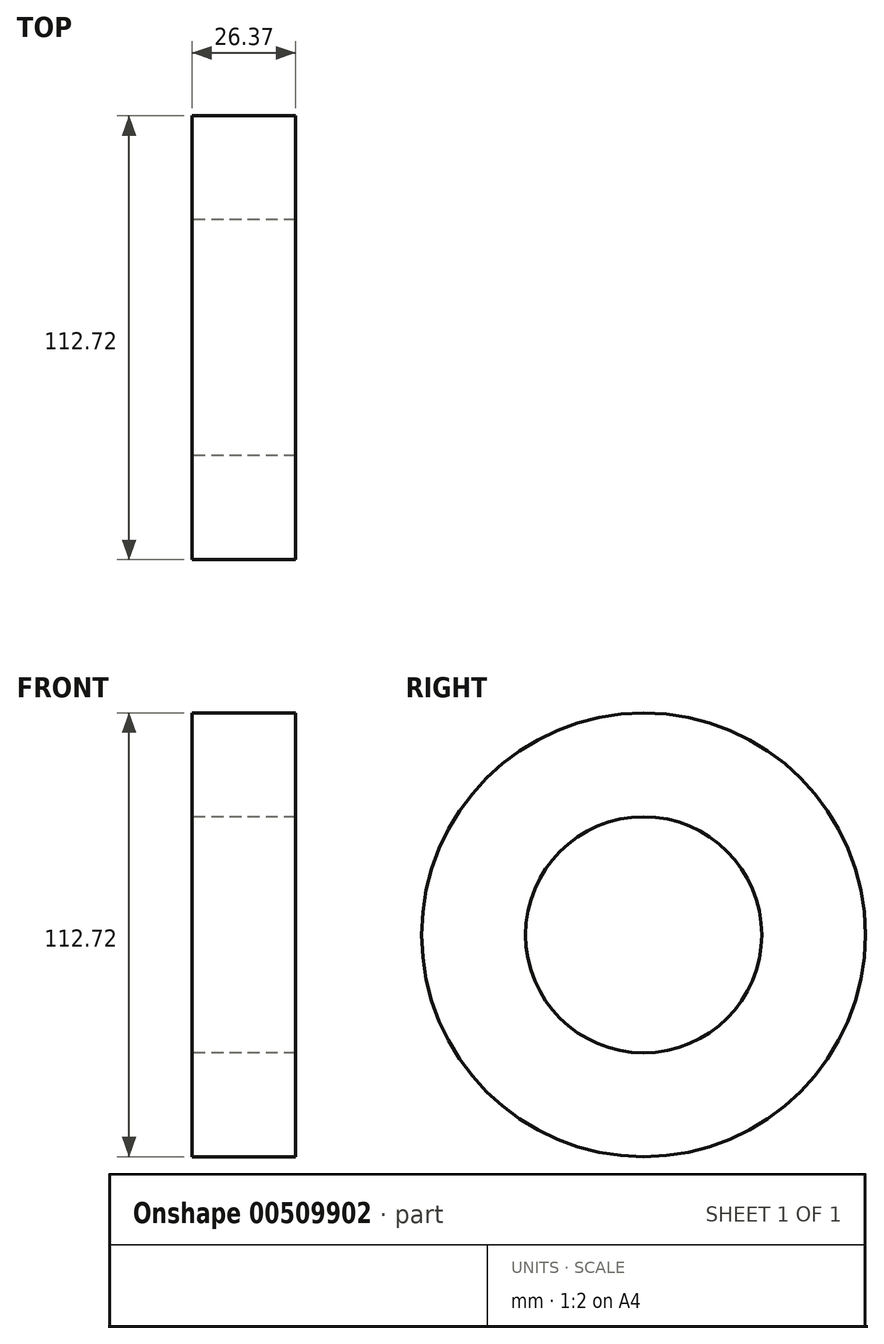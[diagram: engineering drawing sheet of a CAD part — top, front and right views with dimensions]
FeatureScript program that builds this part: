
annotation { "Feature Type Name" : "Feature", "Feature Type Description" : "" }
export const myFeature = defineFeature(function(context is Context, id is Id, definition is map)
    precondition{}
    {
        {
            var Q0;
            Q0=qCreatedBy(makeId("Top.planeOp"),FACE);
            var sketch = newSketch(context, id + "F0", { "sketchPlane" : qUnion([Q0])});
            skLineSegment(sketch, "E0.bottom", {"start": v(-42.99, 24.62) * mm, "end": v(-16.62, 24.62) * mm});
            skLineSegment(sketch, "E0.top", {"start": v(-42.99, -1.74) * mm, "end": v(-16.62, -1.74) * mm});
            skLineSegment(sketch, "E0.left", {"start": v(-42.99, 24.62) * mm, "end": v(-42.99, -1.74) * mm});
            skLineSegment(sketch, "E0.right", {"start": v(-16.62, 24.62) * mm, "end": v(-16.62, -1.74) * mm});
            skLineSegment(sketch, "E1", {"start": v(-89, -31.74) * mm, "end": v(59.78, -31.74) * mm, "construction": true});
            skSolve(sketch);
        }
        {
            var Q0;
            Q0=qSketchRegion(id+"F0",true);
            var Q1;
            Q1=sQuery(id+"F0.wireOp",EDGE,"E1");
            revolve(context, id + "F1", {"entities" : qUnion([Q0]), "axis" : qUnion([Q1]), "revolveType" : RevolveType.FULL});
        }
    });
